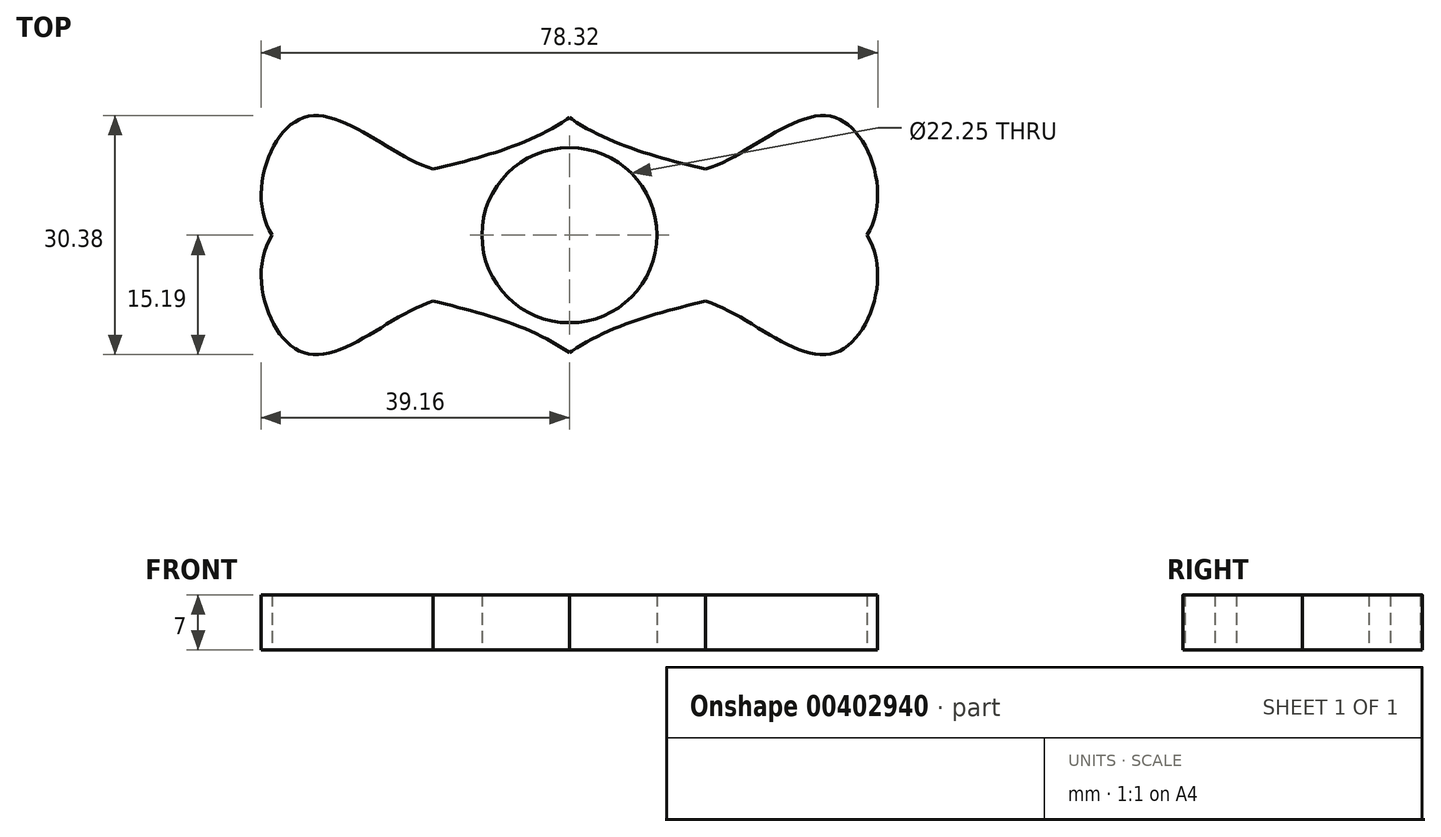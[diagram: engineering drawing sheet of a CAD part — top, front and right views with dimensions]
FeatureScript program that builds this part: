
annotation { "Feature Type Name" : "Feature", "Feature Type Description" : "" }
export const myFeature = defineFeature(function(context is Context, id is Id, definition is map)
    precondition{}
    {
        {
            var Q0;
            Q0=qCreatedBy(makeId("Top.planeOp"),FACE);
            var sketch = newSketch(context, id + "F0", { "sketchPlane" : qUnion([Q0])});
            skCircle(sketch, "E0", {"center": v(0, 0) * mm, "radius": 11.12 * mm});
            skLineSegment(sketch, "E1", {"start": v(0, 11.12) * mm, "end": v(0, 14.94) * mm});
            skLineSegment(sketch, "E2.MirrorCS", {"start": v(0, -11.12) * mm, "end": v(0, -14.94) * mm});
            skFitSpline(sketch, "E3", {"points": [v(0, 14.94) * mm, v(-17.5, 8.45) * mm, v(-33.79, 14.94) * mm, v(-37.78, 0) * mm, v(0, -14.94) * mm], "startDerivative": vector(-96.09, -66.81) * mm, "endDerivative": vector(100.5, -71.09) * mm});
            skFitSpline(sketch, "E4.MirrorCS", {"points": [v(0, 14.94) * mm, v(17.5, 8.45) * mm, v(33.79, 14.94) * mm, v(37.78, 0) * mm, v(0, -14.94) * mm], "startDerivative": vector(96.09, -66.81) * mm, "endDerivative": vector(-100.5, -71.09) * mm});
            skFitSpline(sketch, "E5.MirrorCS", {"points": [v(0, -14.94) * mm, v(-17.5, -8.45) * mm, v(-33.79, -14.94) * mm, v(-37.78, 0) * mm, v(0, 14.94) * mm], "startDerivative": vector(-96.09, 66.81) * mm, "endDerivative": vector(100.5, 71.09) * mm});
            skFitSpline(sketch, "E6.MirrorCS", {"points": [v(0, -14.94) * mm, v(17.5, -8.45) * mm, v(33.79, -14.94) * mm, v(37.78, 0) * mm, v(0, 14.94) * mm], "startDerivative": vector(96.09, 66.81) * mm, "endDerivative": vector(-100.5, 71.09) * mm});
            skArc(sketch, "E7", {"start": v(-33.79, 14.94) * mm, "mid": v(-36.94, 0) * mm, "end": v(-33.79, -14.94) * mm});
            skArc(sketch, "E8.trimOffspring", {"start": v(33.79, -14.93) * mm, "mid": v(36.94, 0) * mm, "end": v(33.79, 14.93) * mm});
            skSolve(sketch);
        }
        {
            var Q0;
            Q0 = qSketchRegion(id + "F0", true);
            extrude(context, id + "F1", {"entities" : qUnion([Q0]), "depth" : 7 * mm});
        }
    });
